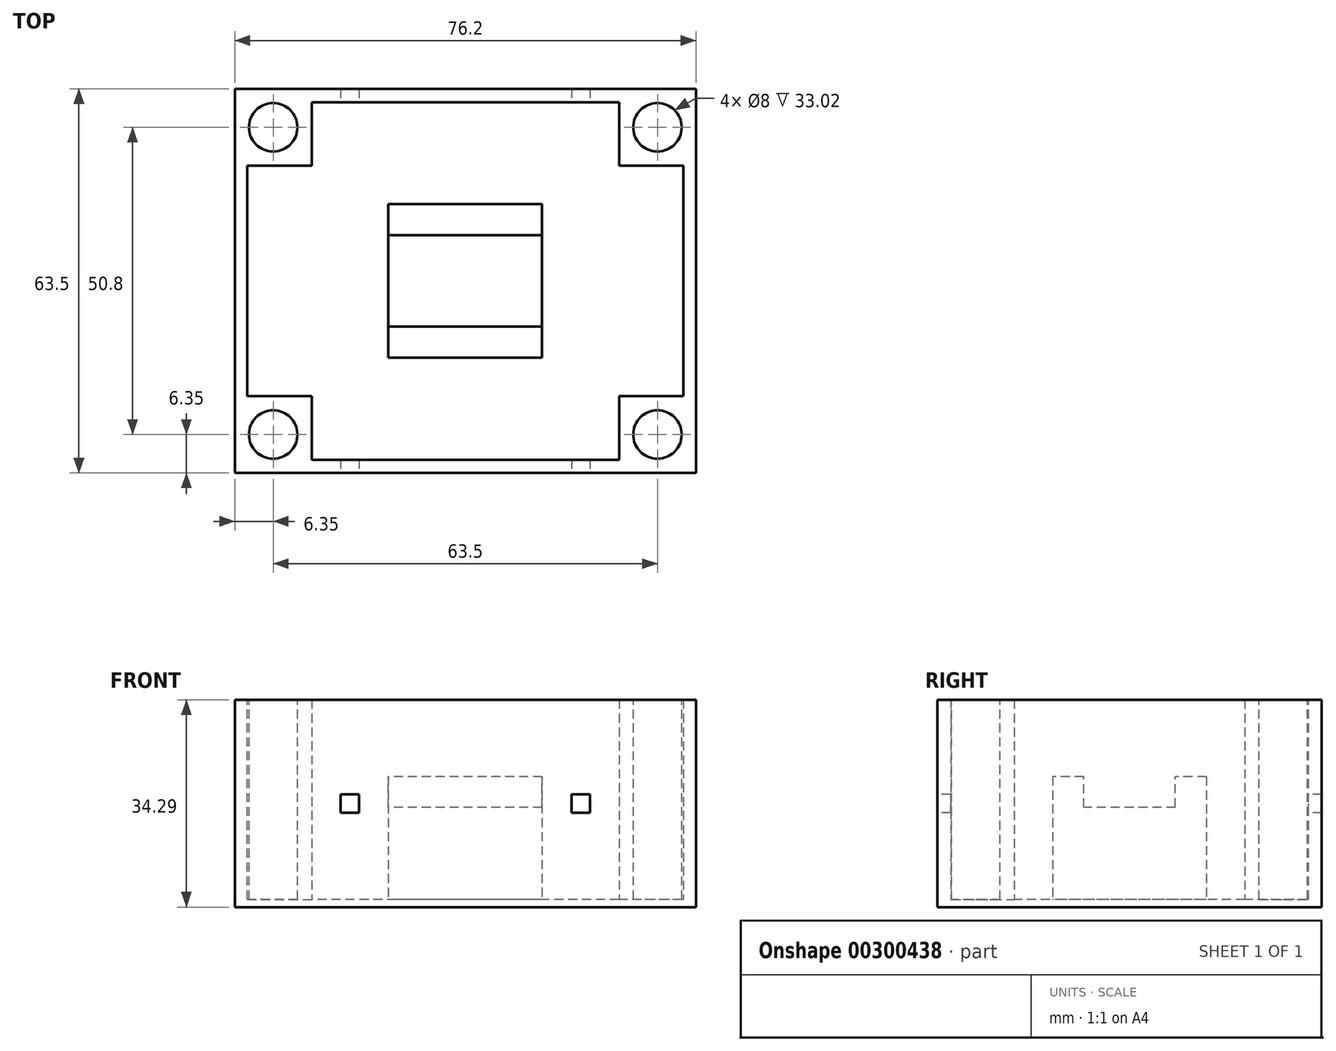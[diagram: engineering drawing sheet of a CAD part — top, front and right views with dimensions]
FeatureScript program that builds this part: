
annotation { "Feature Type Name" : "Feature", "Feature Type Description" : "" }
export const myFeature = defineFeature(function(context is Context, id is Id, definition is map)
    precondition{}
    {
        {
            var Q0;
            Q0=qCreatedBy(makeId("Front.planeOp"),FACE);
            var sketch = newSketch(context, id + "F0", { "sketchPlane" : qUnion([Q0])});
            skLineSegment(sketch, "E0.bottom", {"start": v(38.1, 17.15) * mm, "end": v(-38.1, 17.15) * mm});
            skLineSegment(sketch, "E0.top", {"start": v(38.1, -17.15) * mm, "end": v(-38.1, -17.15) * mm});
            skLineSegment(sketch, "E0.left", {"start": v(38.1, 17.15) * mm, "end": v(38.1, -17.15) * mm});
            skLineSegment(sketch, "E0.right", {"start": v(-38.1, 17.15) * mm, "end": v(-38.1, -17.15) * mm});
            skPoint(sketch, "E0.middle", {"position": v(0, 0) * mm});
            skSolve(sketch);
        }
        {
            var Q0;
            Q0 = qSketchRegion(id + "F0", true);
            extrude(context, id + "F1", {"entities" : qUnion([Q0]), "endBound" : BoundingType.SYMMETRIC, "depth" : 63.5 * mm});
        }
        {
            var Q0;
            Q0=makeQuery(id+"F1.opExtrude","SWEPT_FACE",FACE,{"disambiguationData":[OSD([sQuery(id+"F0.wireOp",EDGE,"E0.bottom")])]});
            var sketch = newSketch(context, id + "F2", { "sketchPlane" : qUnion([Q0])});
            skLineSegment(sketch, "E1.bottom", {"start": v(36.02, 29.56) * mm, "end": v(-36.02, 29.56) * mm});
            skLineSegment(sketch, "E1.top", {"start": v(36.02, -29.56) * mm, "end": v(-36.02, -29.56) * mm});
            skLineSegment(sketch, "E1.left", {"start": v(36.02, 29.56) * mm, "end": v(36.02, -29.56) * mm});
            skLineSegment(sketch, "E1.right", {"start": v(-36.02, 29.56) * mm, "end": v(-36.02, -29.56) * mm});
            skPoint(sketch, "E1.middle", {"position": v(0, 0) * mm});
            skSolve(sketch);
        }
        {
            var Q0;
            Q0 = qSketchRegion(id + "F2", true);
            extrude(context, id + "F3", {"entities" : qUnion([Q0]), "operationType" : NewBodyOperationType.REMOVE, "oppositeDirection" : true, "depth" : 33.02 * mm});
        }
        {
            var Q0;
            Q0=makeQuery(id+"F1.opExtrude","CAP_FACE",FACE,{"disambiguationData":[OSD([sQuery(id+"F0.wireOp",EDGE,"E0.bottom"),sQuery(id+"F0.wireOp",EDGE,"E0.top"),sQuery(id+"F0.wireOp",EDGE,"E0.left"),sQuery(id+"F0.wireOp",EDGE,"E0.right")])],"isStart":false});
            var sketch = newSketch(context, id + "F4", { "sketchPlane" : qUnion([Q0])});
            skLineSegment(sketch, "E2", {"start": v(-38.1, 0) * mm, "end": v(38.1, 0) * mm});
            skLineSegment(sketch, "E3", {"start": v(38.1, 0) * mm, "end": v(0, 0) * mm});
            skLineSegment(sketch, "E4", {"start": v(0, 0) * mm, "end": v(-38.1, 0) * mm});
            skLineSegment(sketch, "E5.bottom", {"start": v(-17.53, 1.52) * mm, "end": v(-20.57, 1.52) * mm});
            skLineSegment(sketch, "E5.top", {"start": v(-17.53, -1.52) * mm, "end": v(-20.57, -1.52) * mm});
            skLineSegment(sketch, "E5.left", {"start": v(-17.53, 1.52) * mm, "end": v(-17.53, -1.52) * mm});
            skLineSegment(sketch, "E5.right", {"start": v(-20.57, 1.52) * mm, "end": v(-20.57, -1.52) * mm});
            skPoint(sketch, "E5.middle", {"position": v(-19.05, 0) * mm});
            skLineSegment(sketch, "E6.bottom", {"start": v(20.57, 1.52) * mm, "end": v(17.53, 1.52) * mm});
            skLineSegment(sketch, "E6.top", {"start": v(20.57, -1.52) * mm, "end": v(17.53, -1.52) * mm});
            skLineSegment(sketch, "E6.left", {"start": v(20.57, 1.52) * mm, "end": v(20.57, -1.52) * mm});
            skLineSegment(sketch, "E6.right", {"start": v(17.53, 1.52) * mm, "end": v(17.53, -1.52) * mm});
            skPoint(sketch, "E6.middle", {"position": v(19.05, 0) * mm});
            skSolve(sketch);
        }
        {
            var Q0;
            Q0 = qSketchRegion(id + "F4", true);
            extrude(context, id + "F5", {"entities" : qUnion([Q0]), "operationType" : NewBodyOperationType.REMOVE, "oppositeDirection" : true, "depth" : 76.2 * mm});
        }
        {
            var Q0;
            Q0=makeQuery(id+"F1.opExtrude","SWEPT_FACE",FACE,{"disambiguationData":[OSD([sQuery(id+"F0.wireOp",EDGE,"E0.bottom")])]});
            var sketch = newSketch(context, id + "F6", { "sketchPlane" : qUnion([Q0])});
            skLineSegment(sketch, "E7.bottom", {"start": v(-38.1, 31.75) * mm, "end": v(-25.4, 31.75) * mm});
            skLineSegment(sketch, "E7.top", {"start": v(-38.1, 19.05) * mm, "end": v(-25.4, 19.05) * mm});
            skLineSegment(sketch, "E7.left", {"start": v(-38.1, 31.75) * mm, "end": v(-38.1, 19.05) * mm});
            skLineSegment(sketch, "E7.right", {"start": v(-25.4, 31.75) * mm, "end": v(-25.4, 19.05) * mm});
            skLineSegment(sketch, "E8.bottom", {"start": v(-38.1, -31.75) * mm, "end": v(-25.4, -31.75) * mm});
            skLineSegment(sketch, "E8.top", {"start": v(-38.1, -19.05) * mm, "end": v(-25.4, -19.05) * mm});
            skLineSegment(sketch, "E8.left", {"start": v(-38.1, -31.75) * mm, "end": v(-38.1, -19.05) * mm});
            skLineSegment(sketch, "E8.right", {"start": v(-25.4, -31.75) * mm, "end": v(-25.4, -19.05) * mm});
            skLineSegment(sketch, "E9.bottom", {"start": v(38.1, -31.75) * mm, "end": v(25.4, -31.75) * mm});
            skLineSegment(sketch, "E9.top", {"start": v(38.1, -19.05) * mm, "end": v(25.4, -19.05) * mm});
            skLineSegment(sketch, "E9.left", {"start": v(38.1, -31.75) * mm, "end": v(38.1, -19.05) * mm});
            skLineSegment(sketch, "E9.right", {"start": v(25.4, -31.75) * mm, "end": v(25.4, -19.05) * mm});
            skLineSegment(sketch, "E10.bottom", {"start": v(38.1, 31.75) * mm, "end": v(25.4, 31.75) * mm});
            skLineSegment(sketch, "E10.top", {"start": v(38.1, 19.05) * mm, "end": v(25.4, 19.05) * mm});
            skLineSegment(sketch, "E10.left", {"start": v(38.1, 31.75) * mm, "end": v(38.1, 19.05) * mm});
            skLineSegment(sketch, "E10.right", {"start": v(25.4, 31.75) * mm, "end": v(25.4, 19.05) * mm});
            skLineSegment(sketch, "E11", {"start": v(-25.4, 19.05) * mm, "end": v(-38.1, 31.75) * mm});
            skLineSegment(sketch, "E12", {"start": v(25.4, 19.05) * mm, "end": v(38.1, 31.75) * mm});
            skLineSegment(sketch, "E13", {"start": v(38.1, -31.75) * mm, "end": v(25.4, -19.05) * mm});
            skLineSegment(sketch, "E14", {"start": v(-25.4, -19.05) * mm, "end": v(-38.1, -31.75) * mm});
            skCircle(sketch, "E15", {"center": v(-31.75, 25.4) * mm, "radius": 4 * mm});
            skCircle(sketch, "E16", {"center": v(31.75, 25.4) * mm, "radius": 4 * mm});
            skCircle(sketch, "E17", {"center": v(-31.75, -25.4) * mm, "radius": 4 * mm});
            skCircle(sketch, "E18", {"center": v(31.75, -25.4) * mm, "radius": 4 * mm});
            skSolve(sketch);
        }
        {
            var Q0;
            Q0 = qSketchRegion(id + "F6", true);
            extrude(context, id + "F7", {"entities" : qUnion([Q0]), "operationType" : NewBodyOperationType.ADD, "oppositeDirection" : true, "depth" : 33.02 * mm});
        }
        {
            var Q0;
            {var subQ0=sQuery(id+"F2.wireOp",EDGE,"E1.bottom");var subQ1=sQuery(id+"F2.wireOp",EDGE,"E1.top");var subQ2=sQuery(id+"F2.wireOp",EDGE,"E1.left");var subQ3=sQuery(id+"F2.wireOp",EDGE,"E1.right");Q0=makeQuery(id+"F7.boolean.opBoolean","SPLIT",FACE,{"disambiguationData":[TD([makeQuery(id+"F3.boolean.opBoolean","COPY",FACE,{"derivedFrom":makeQuery(id+"F3.opExtrude","SWEPT_FACE",FACE,{"disambiguationData":[OSD([subQ0])]})})])],"derivedFrom":makeQuery(id+"F3.boolean.opBoolean","COPY",FACE,{"derivedFrom":makeQuery(id+"F3.opExtrude","CAP_FACE",FACE,{"disambiguationData":[OSD([subQ0,subQ1,subQ2,subQ3])],"isStart":false})})});}
            var sketch = newSketch(context, id + "F8", { "sketchPlane" : qUnion([Q0])});
            skLineSegment(sketch, "E19.bottom", {"start": v(12.7, 12.7) * mm, "end": v(-12.7, 12.7) * mm});
            skLineSegment(sketch, "E19.top", {"start": v(12.7, -12.7) * mm, "end": v(-12.7, -12.7) * mm});
            skLineSegment(sketch, "E19.left", {"start": v(12.7, 12.7) * mm, "end": v(12.7, -12.7) * mm});
            skLineSegment(sketch, "E19.right", {"start": v(-12.7, 12.7) * mm, "end": v(-12.7, -12.7) * mm});
            skPoint(sketch, "E19.middle", {"position": v(0, 0) * mm});
            skSolve(sketch);
        }
        {
            var Q0;
            Q0 = qSketchRegion(id + "F8", true);
            extrude(context, id + "F9", {"entities" : qUnion([Q0]), "operationType" : NewBodyOperationType.ADD, "depth" : 20.32 * mm});
        }
        {
            var Q0;
            Q0=makeQuery(id+"F9.opExtrude","CAP_FACE",FACE,{"disambiguationData":[OSD([sQuery(id+"F8.wireOp",EDGE,"E19.bottom"),sQuery(id+"F8.wireOp",EDGE,"E19.top"),sQuery(id+"F8.wireOp",EDGE,"E19.left"),sQuery(id+"F8.wireOp",EDGE,"E19.right")])],"isStart":false});
            var sketch = newSketch(context, id + "F10", { "sketchPlane" : qUnion([Q0])});
            skLineSegment(sketch, "E20.bottom", {"start": v(12.7, 7.57) * mm, "end": v(-12.7, 7.57) * mm});
            skLineSegment(sketch, "E20.top", {"start": v(12.7, -7.57) * mm, "end": v(-12.7, -7.57) * mm});
            skLineSegment(sketch, "E20.left", {"start": v(12.7, 7.57) * mm, "end": v(12.7, -7.57) * mm});
            skLineSegment(sketch, "E20.right", {"start": v(-12.7, 7.57) * mm, "end": v(-12.7, -7.57) * mm});
            skPoint(sketch, "E20.middle", {"position": v(0, 0) * mm});
            skSolve(sketch);
        }
        {
            var Q0;
            Q0 = qSketchRegion(id + "F10", true);
            extrude(context, id + "F11", {"entities" : qUnion([Q0]), "operationType" : NewBodyOperationType.REMOVE, "oppositeDirection" : true, "depth" : 5.08 * mm});
        }
    });
